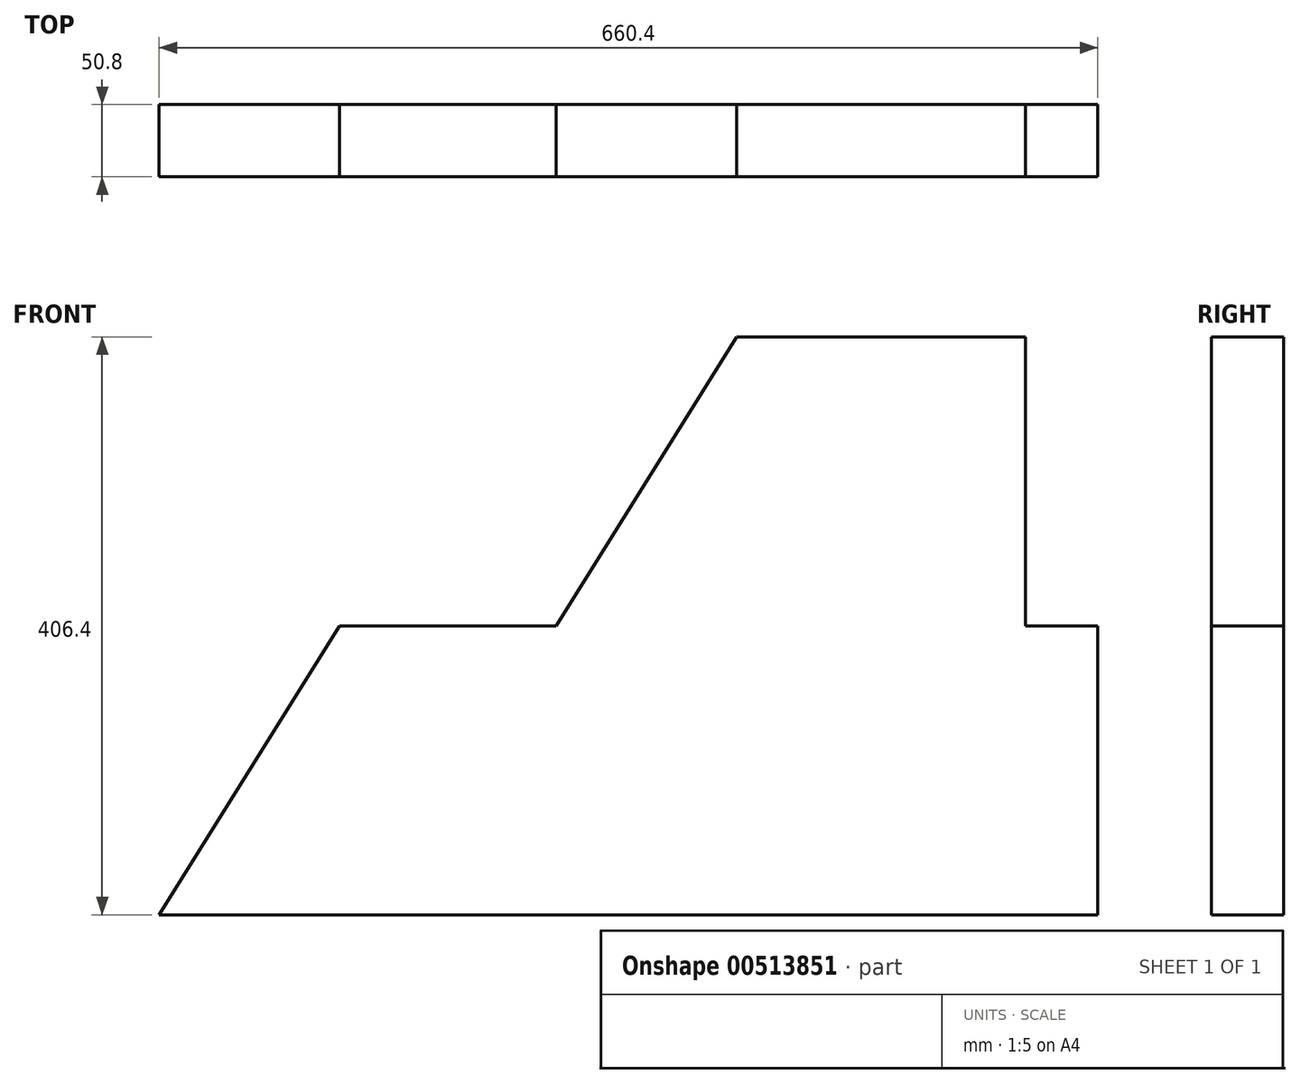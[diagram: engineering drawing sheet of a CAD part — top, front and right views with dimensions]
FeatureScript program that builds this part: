
annotation { "Feature Type Name" : "Feature", "Feature Type Description" : "" }
export const myFeature = defineFeature(function(context is Context, id is Id, definition is map)
    precondition{}
    {
        {
            var Q0;
            Q0=qCreatedBy(makeId("Front.planeOp"),FACE);
            var sketch = newSketch(context, id + "F0", { "sketchPlane" : qUnion([Q0])});
            skLineSegment(sketch, "E0", {"start": v(660.4, 0) * mm, "end": v(0, 0) * mm});
            skLineSegment(sketch, "E1", {"start": v(660.4, 0) * mm, "end": v(660.4, 203.2) * mm});
            skLineSegment(sketch, "E2", {"start": v(551.1, -188.57) * mm, "end": v(523.45, -188.57) * mm});
            skLineSegment(sketch, "E3", {"start": v(660.4, 203.2) * mm, "end": v(609.6, 203.2) * mm});
            skLineSegment(sketch, "E4", {"start": v(609.6, 203.2) * mm, "end": v(609.6, 406.4) * mm});
            skLineSegment(sketch, "E5", {"start": v(609.6, 406.4) * mm, "end": v(406.4, 406.4) * mm});
            skLineSegment(sketch, "E6", {"start": v(406.4, 406.4) * mm, "end": v(279.4, 203.2) * mm});
            skLineSegment(sketch, "E7", {"start": v(279.4, 203.2) * mm, "end": v(127, 203.2) * mm});
            skLineSegment(sketch, "E8", {"start": v(127, 203.2) * mm, "end": v(0, 0) * mm});
            skSolve(sketch);
        }
        {
            var Q0;
            Q0=makeQuery(id+"F0.imprint","IMPRINT",FACE,{"disambiguationData":[TD([[makeQuery(id+"F0.imprint","IMPRINT",EDGE,{"derivedFrom":sQuery(id+"F0.wireOp",EDGE,"E0")}),-1.0]])]});
            extrude(context, id + "F1", {"entities" : qUnion([Q0]), "depth" : 50.8 * mm, "offsetDistance" : 25.4 * mm});
        }
    });
